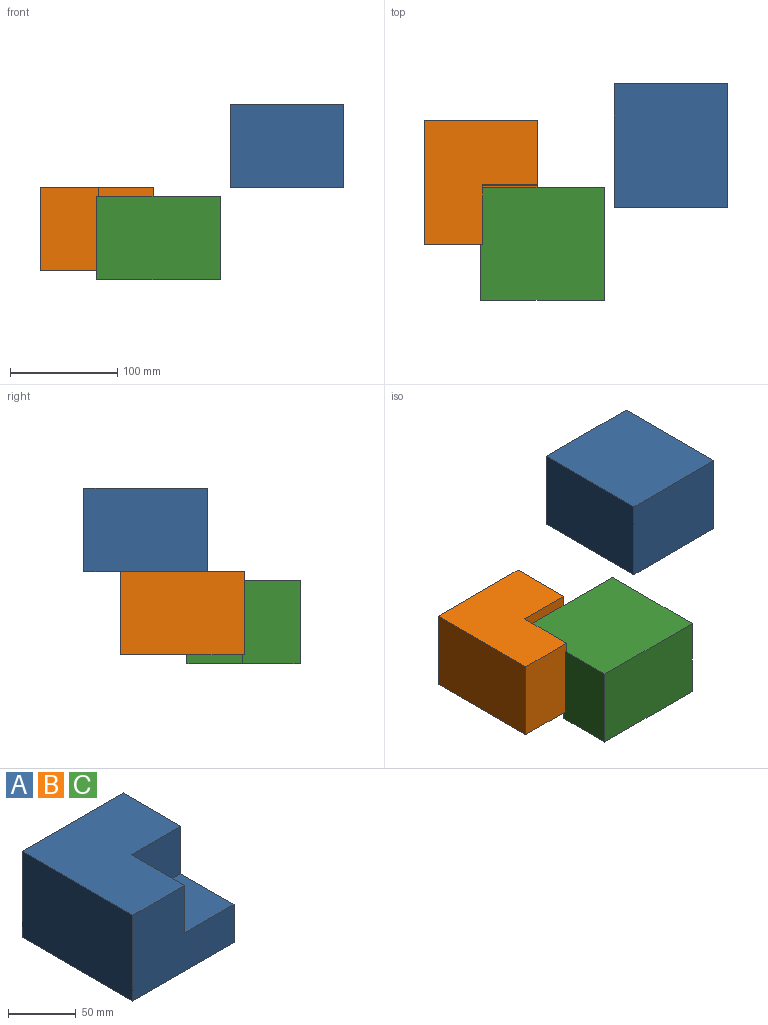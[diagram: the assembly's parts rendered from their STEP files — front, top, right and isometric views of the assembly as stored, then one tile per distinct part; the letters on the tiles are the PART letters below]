
ASSEMBLY  parts=3 mates=2
PART A: 9 faces, bbox 105.5x115.6x77.5 mm
  f0: plane 115.58x77.47mm, normal (1,0,0), area 6580.9mm2, adj f2,f3,f4,f5,f6,f8
  f1: plane 115.58x77.47mm, normal (-1,0,0), area 8954.1mm2, adj f2,f3,f4,f5
  f2: plane 105.45x77.47mm, normal (0,-1,0), area 5958.9mm2, adj f0,f1,f4,f5,f7,f8
  f3: plane 105.45x77.47mm, normal (0,1,0), area 8169.3mm2, adj f0,f1,f4,f5
  f4: plane 115.58x105.45mm, normal (0,0,1), area 9341.2mm2, adj f0,f1,f2,f3,f6,f7
  f5: plane 115.58x105.45mm, normal (0,0,-1), area 12188.1mm2, adj f0,f1,f2,f3
  f6: plane 51.49x42.93mm, normal (0,-1,0), area 2210.4mm2, adj f0,f4,f7,f8
  f7: plane 55.29x42.93mm, normal (1,0,0), area 2373.2mm2, adj f2,f4,f6,f8
  f8: plane 55.29x51.49mm, normal (0,0,1), area 2846.9mm2, adj f0,f2,f6,f7
PART B: same geometry as A
PART C: same geometry as A
PLACE A rot(axis=(1,0,0),180deg) t=(163.52,152.18,156.54)mm
PLACE B t=(-13.11,2.68,1.6)mm fixed
PLACE C rot(axis=(0.71,0.71,0),180deg) t=(38.95,-49.38,70.69)mm
MATE planar A.f4 <-> B.f4  axis (0,0,-1) through (208.02,85.2,79.07)mm
MATE cylindrical C.f8 <-> B.f8  axis (0,0,-1) through (66.59,30.32,36.14)mm
